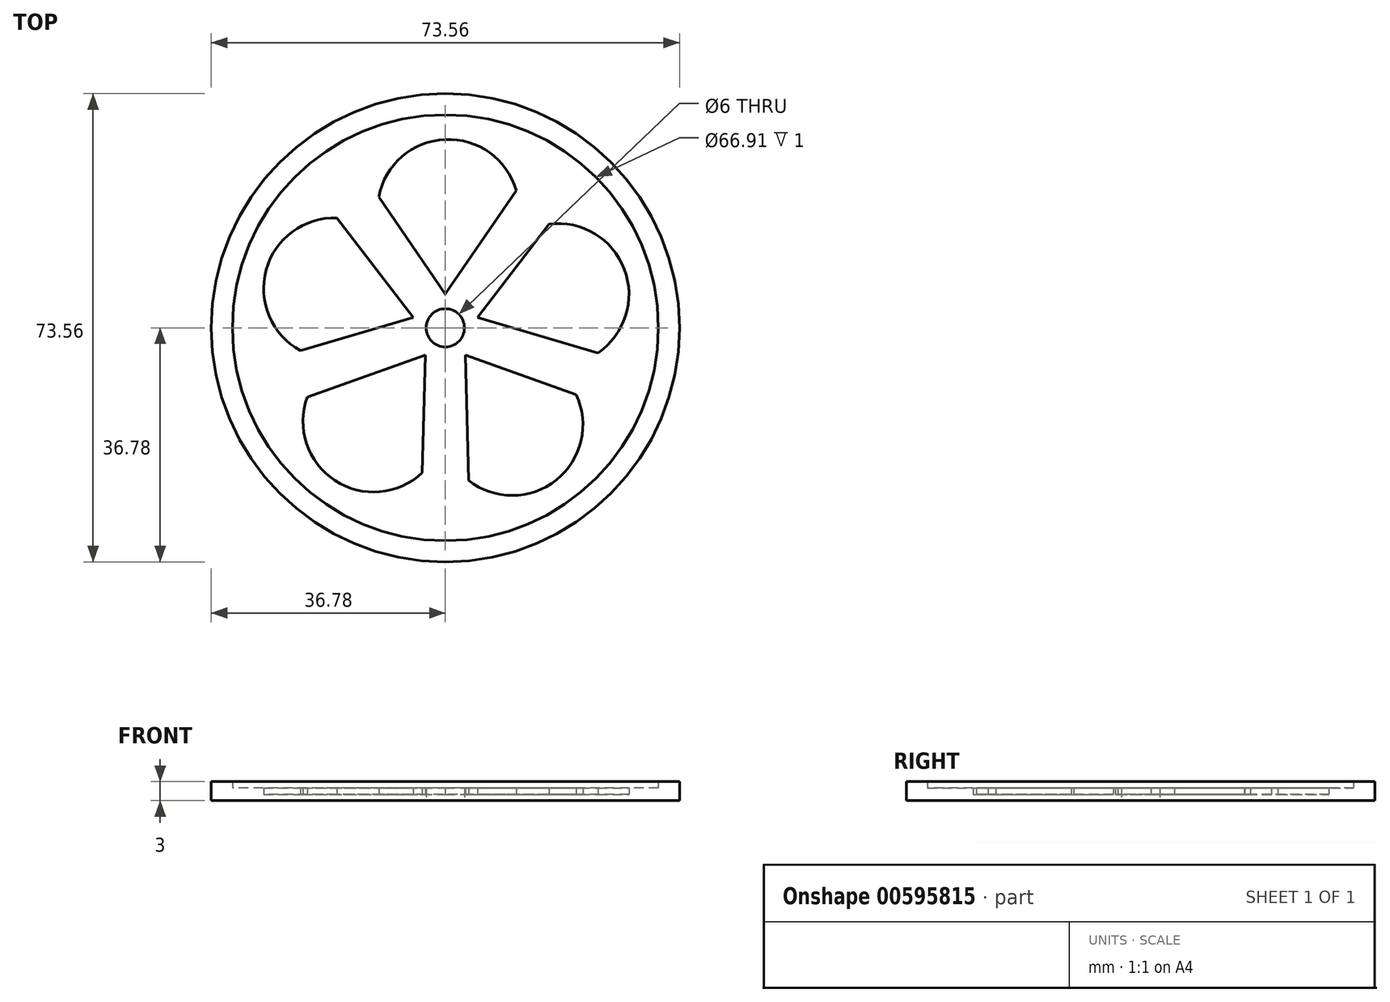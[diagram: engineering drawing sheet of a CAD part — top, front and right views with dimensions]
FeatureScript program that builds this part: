
annotation { "Feature Type Name" : "Feature", "Feature Type Description" : "" }
export const myFeature = defineFeature(function(context is Context, id is Id, definition is map)
    precondition{}
    {
        {
            var Q0;
            Q0=qCreatedBy(makeId("Top.planeOp"),FACE);
            var sketch = newSketch(context, id + "F0", { "sketchPlane" : qUnion([Q0])});
            skLineSegment(sketch, "E0.bottom", {"start": v(0, 75) * mm, "end": v(75, 75) * mm, "construction": true});
            skLineSegment(sketch, "E0.top", {"start": v(0, 0) * mm, "end": v(75, 0) * mm, "construction": true});
            skLineSegment(sketch, "E0.left", {"start": v(0, 75) * mm, "end": v(0, 0) * mm, "construction": true});
            skLineSegment(sketch, "E0.right", {"start": v(75, 75) * mm, "end": v(75, 0) * mm, "construction": true});
            skLineSegment(sketch, "E1", {"start": v(0, 75) * mm, "end": v(75, 0) * mm, "construction": true});
            skCircle(sketch, "E2", {"center": v(37.5, 37.5) * mm, "radius": 3 * mm});
            skCircle(sketch, "E3", {"center": v(37.5, 37.5) * mm, "radius": 36.78 * mm});
            skLineSegment(sketch, "E4", {"start": v(27.04, 58.06) * mm, "end": v(37.5, 42.8) * mm});
            skLineSegment(sketch, "E5", {"start": v(37.5, 42.8) * mm, "end": v(48.65, 59.06) * mm});
            skArc(sketch, "E6", {"start": v(48.65, 59.06) * mm, "mid": v(37.45, 67.09) * mm, "end": v(27.04, 58.06) * mm});
            skCircle(sketch, "E7", {"center": v(37.5, 37.5) * mm, "radius": 33.45 * mm});
            skArc(sketch, "E8.1.0", {"start": v(20.44, 54.76) * mm, "mid": v(9.34, 46.6) * mm, "end": v(14.72, 33.9) * mm});
            skLineSegment(sketch, "E8.1.1", {"start": v(32.45, 39.14) * mm, "end": v(20.44, 54.76) * mm});
            skLineSegment(sketch, "E8.1.2", {"start": v(14.72, 33.9) * mm, "end": v(32.45, 39.14) * mm});
            skArc(sketch, "E8.2.0", {"start": v(15.8, 26.6) * mm, "mid": v(20.15, 13.53) * mm, "end": v(33.88, 14.72) * mm});
            skLineSegment(sketch, "E8.2.1", {"start": v(34.38, 33.2) * mm, "end": v(15.8, 26.6) * mm});
            skLineSegment(sketch, "E8.2.2", {"start": v(33.88, 14.72) * mm, "end": v(34.38, 33.2) * mm});
            skLineSegment(sketch, "E9.4.3.0", {"start": v(40.62, 33.2) * mm, "end": v(41.16, 13.5) * mm});
            skArc(sketch, "E9.5.3.0", {"start": v(41.16, 13.5) * mm, "mid": v(54.93, 13.6) * mm, "end": v(58.04, 27.02) * mm});
            skLineSegment(sketch, "E9.7.3.0", {"start": v(58.04, 27.02) * mm, "end": v(40.62, 33.2) * mm});
            skLineSegment(sketch, "E9.4.4.0", {"start": v(42.55, 39.14) * mm, "end": v(61.45, 33.56) * mm});
            skArc(sketch, "E9.5.4.0", {"start": v(61.45, 33.56) * mm, "mid": v(65.62, 46.7) * mm, "end": v(53.82, 53.8) * mm});
            skLineSegment(sketch, "E9.7.4.0", {"start": v(53.82, 53.8) * mm, "end": v(42.55, 39.14) * mm});
            skSolve(sketch);
        }
        {
            var Q0;
            Q0 = qSketchRegion(id + "F0", true);
            var Q1;
            Q1=makeQuery(id+"F0.imprint","IMPRINT",FACE,{"disambiguationData":[TD([[makeQuery(id+"F0.imprint","IMPRINT",EDGE,{"derivedFrom":sQuery(id+"F0.wireOp",EDGE,"E2")}),-1.0]])]});
            extrude(context, id + "F1", {"entities" : qUnion([Q0, Q1]), "depth" : 2 * mm, "offsetDistance" : 25 * mm});
        }
        {
            var Q0;
            Q0 = qSketchRegion(id + "F0", true);
            extrude(context, id + "F2", {"entities" : qUnion([Q0]), "operationType" : NewBodyOperationType.ADD, "depth" : 3 * mm, "offsetDistance" : 25 * mm});
        }
        {
            var Q0;
            Q0=makeQuery(id+"F0.imprint","IMPRINT",FACE,{"disambiguationData":[TD([[makeQuery(id+"F0.imprint","IMPRINT",EDGE,{"derivedFrom":sQuery(id+"F0.wireOp",EDGE,"E8.1.0")}),1.0]])]});
            var Q1;
            Q1=makeQuery(id+"F0.imprint","IMPRINT",FACE,{"disambiguationData":[TD([[makeQuery(id+"F0.imprint","IMPRINT",EDGE,{"derivedFrom":sQuery(id+"F0.wireOp",EDGE,"E4")}),1.0]])]});
            var Q2;
            Q2=makeQuery(id+"F0.imprint","IMPRINT",FACE,{"disambiguationData":[TD([[makeQuery(id+"F0.imprint","IMPRINT",EDGE,{"derivedFrom":sQuery(id+"F0.wireOp",EDGE,"E9.4.4.0")}),1.0]])]});
            var Q3;
            Q3=makeQuery(id+"F0.imprint","IMPRINT",FACE,{"disambiguationData":[TD([[makeQuery(id+"F0.imprint","IMPRINT",EDGE,{"derivedFrom":sQuery(id+"F0.wireOp",EDGE,"E9.4.3.0")}),1.0]])]});
            var Q4;
            Q4=makeQuery(id+"F0.imprint","IMPRINT",FACE,{"disambiguationData":[TD([[makeQuery(id+"F0.imprint","IMPRINT",EDGE,{"derivedFrom":sQuery(id+"F0.wireOp",EDGE,"E8.2.0")}),1.0]])]});
            extrude(context, id + "F3", {"entities" : qUnion([Q0, Q1, Q2, Q3, Q4]), "operationType" : NewBodyOperationType.ADD, "depth" : 1 * mm, "offsetDistance" : 25 * mm});
        }
    });
